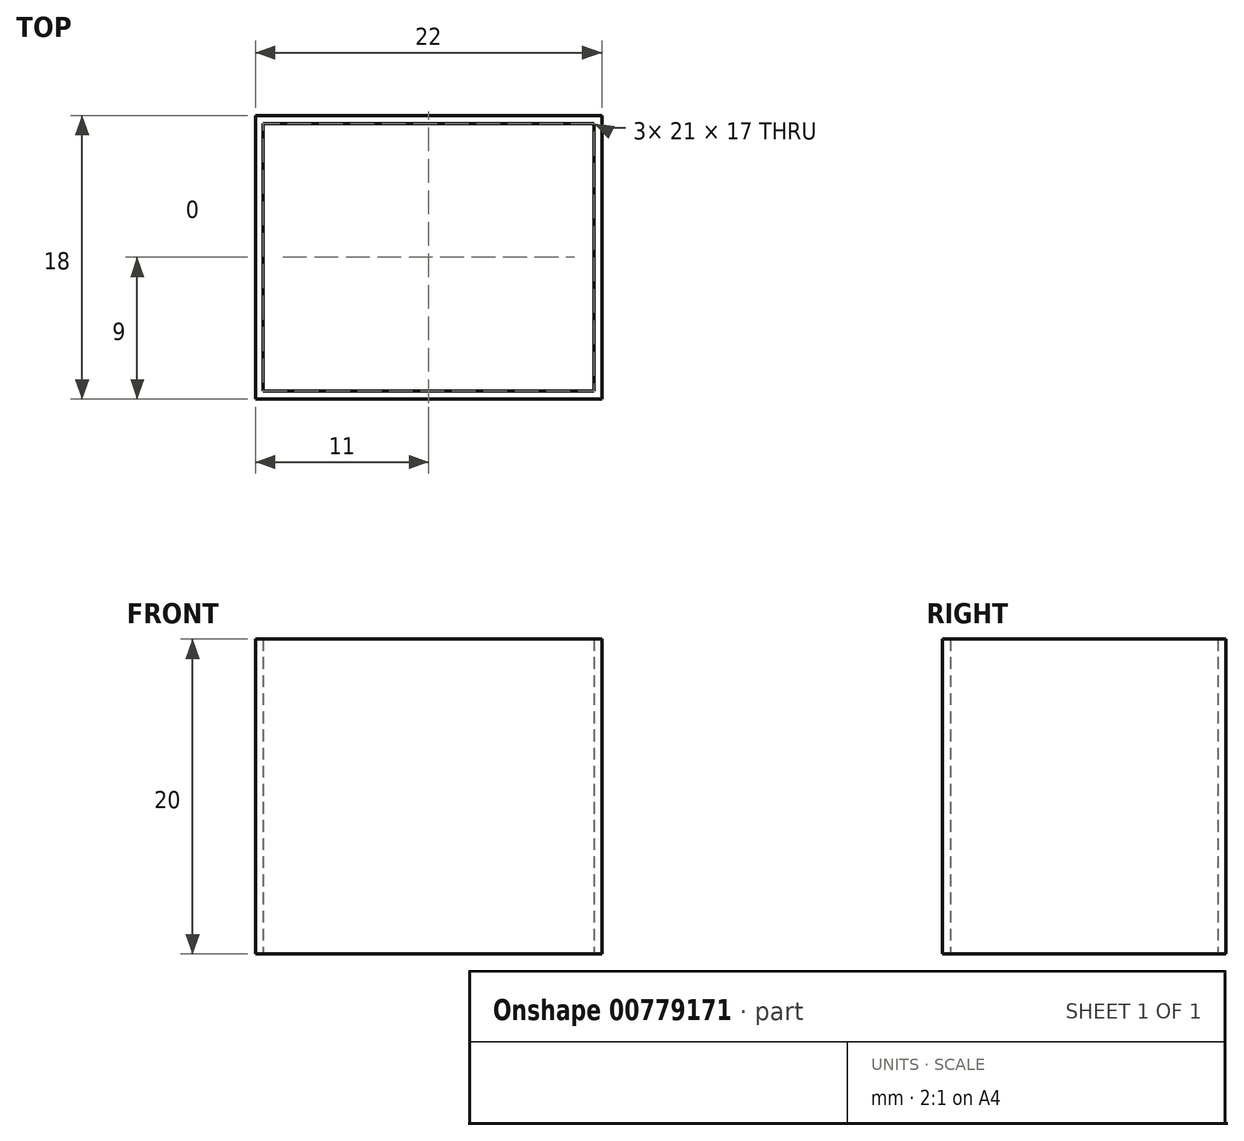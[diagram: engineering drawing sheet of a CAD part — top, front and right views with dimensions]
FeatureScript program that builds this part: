
annotation { "Feature Type Name" : "Feature", "Feature Type Description" : "" }
export const myFeature = defineFeature(function(context is Context, id is Id, definition is map)
    precondition{}
    {
        {
            var Q0;
            Q0=qCreatedBy(makeId("Top.planeOp"),FACE);
            var sketch = newSketch(context, id + "F0", { "sketchPlane" : qUnion([Q0])});
            skLineSegment(sketch, "E0.bottom", {"start": v(0, 0) * mm, "end": v(22, 0) * mm});
            skLineSegment(sketch, "E0.top", {"start": v(0, -18) * mm, "end": v(22, -18) * mm});
            skLineSegment(sketch, "E0.left", {"start": v(0, 0) * mm, "end": v(0, -18) * mm});
            skLineSegment(sketch, "E0.right", {"start": v(22, 0) * mm, "end": v(22, -18) * mm});
            skLineSegment(sketch, "E1.bottom", {"start": v(0.5, -0.5) * mm, "end": v(21.5, -0.5) * mm});
            skLineSegment(sketch, "E1.top", {"start": v(0.5, -17.5) * mm, "end": v(21.5, -17.5) * mm});
            skLineSegment(sketch, "E1.left", {"start": v(0.5, -0.5) * mm, "end": v(0.5, -17.5) * mm});
            skLineSegment(sketch, "E1.right", {"start": v(21.5, -0.5) * mm, "end": v(21.5, -17.5) * mm});
            skSolve(sketch);
        }
        {
            var Q0;
            Q0=makeQuery(id+"F0.imprint","IMPRINT",FACE,{"disambiguationData":[TD([[makeQuery(id+"F0.imprint","IMPRINT",EDGE,{"derivedFrom":sQuery(id+"F0.wireOp",EDGE,"E0.bottom")}),-1.0]])]});
            extrude(context, id + "F1", {"entities" : qUnion([Q0]), "depth" : 20 * mm, "offsetDistance" : 25 * mm});
        }
    });
